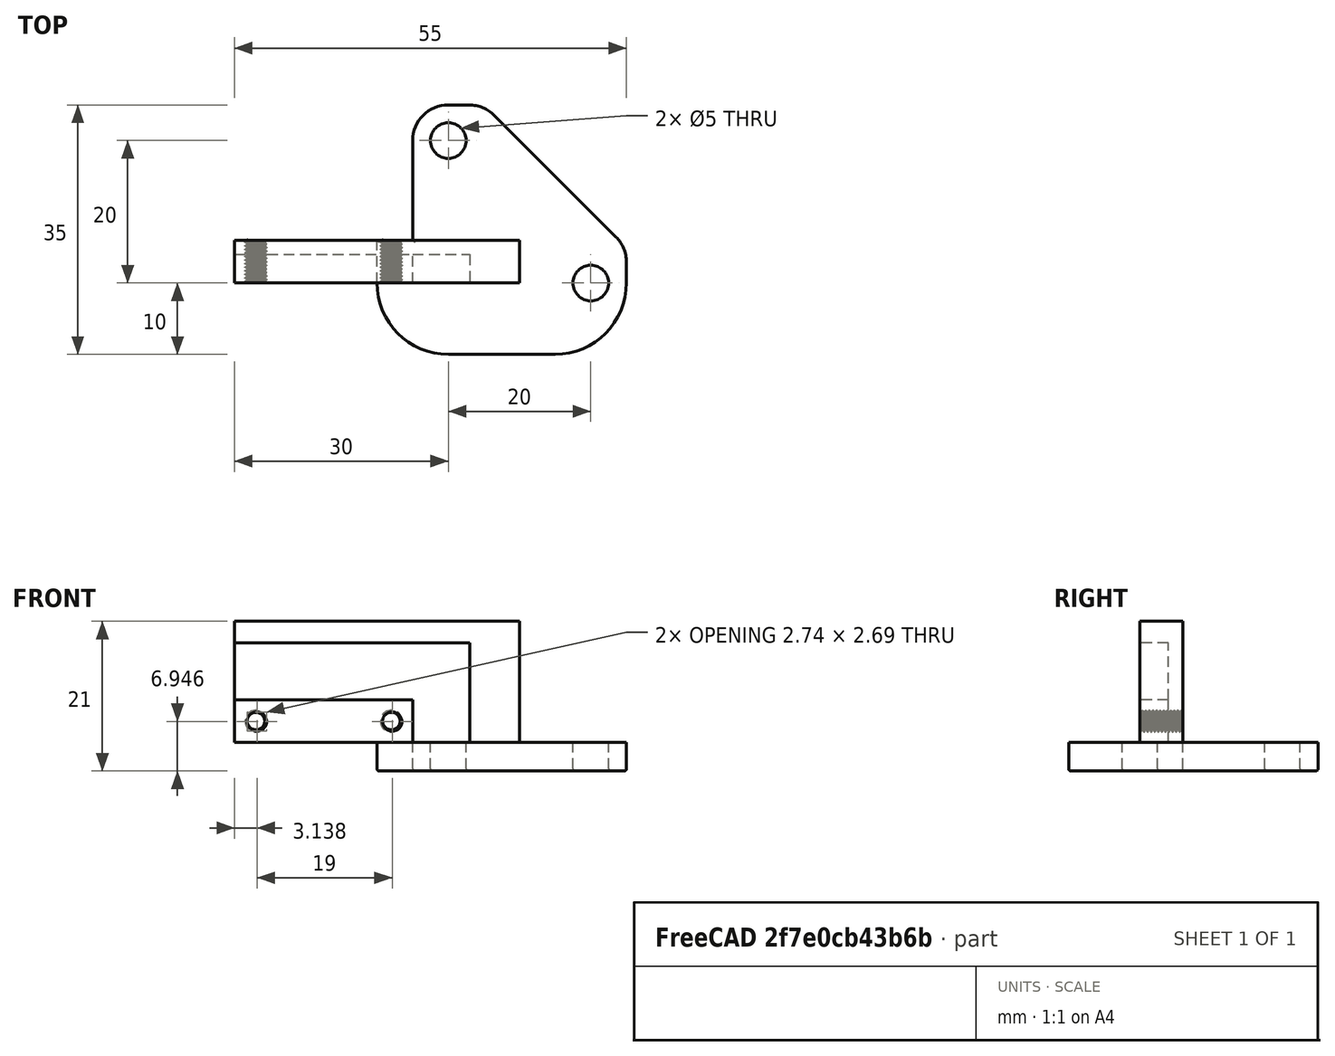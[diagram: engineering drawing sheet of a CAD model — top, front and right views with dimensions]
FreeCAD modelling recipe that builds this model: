
FCSTD DOCUMENT  (FreeCAD 0.18R16146 (Git))
Label: Y_DriveEndschalter_rechts_Ver3
License: All rights reserved
LicenseURL: http://en.wikipedia.org/wiki/All_rights_reserved
objects: Part::Cut×8, Part::Box×6, Part::Fillet×4, Part::Feature×2, Part::Cylinder×2, Part::Chamfer×1, Part::MultiFuse×1
note: 24 computed .brp shape members not serialized (recipe doc carries the construction recipe); baked Part::Feature solids carry a one-line shape summary decoded from their .brp

FEATURE [Part::Box] Box  label="Cube"
  AttacherType = Attacher::AttachEngine3D
  Height = 6
  Length = 40
  Width = 17
FEATURE [Part::Box] Box001  label="Cube001"
  AttacherType = Attacher::AttachEngine3D
  Height = 10
  Length = 33
  Placement = pos=(0,6,2) rot=(0,0,1;0rad)
  Width = 8
FEATURE [Part::Box] Box002  label="Cube002"
  AttacherType = Attacher::AttachEngine3D
  Height = 10
  Length = 8
  Placement = pos=(25,0,2) rot=(0,0,1;0rad)
  Width = 14
FEATURE [Part::Feature] Part__Feature  label="ScrewTap-M3x50_"
  Placement = pos=(3,3,8) rot=(0,0,1;0rad)
  shape: bbox 4.303 x 4.617 x 51.5 mm, 410 faces (baked)
FEATURE [Part::Feature] Part__Feature001  label="ScrewTap-M3x50_001"
  Placement = pos=(22,3,8) rot=(0,0,1;0rad)
  shape: bbox 4.303 x 4.617 x 51.5 mm, 410 faces (baked)
FEATURE [Part::Cut] Cut
  Base = -> Box
  Tool = -> Box001
FEATURE [Part::Cut] Cut001
  Base = -> Cut
  Tool = -> Box002
FEATURE [Part::Cut] Cut002
  Base = -> Cut001
  Tool = -> Part__Feature001
FEATURE [Part::Cut] Cut003
  Base = -> Cut002
  Placement = pos=(-10,16,4) rot=(1,0,0;1.5708rad)
  Tool = -> Part__Feature
FEATURE [Part::Box] Box003  label="Cube003"
  AttacherType = Attacher::AttachEngine3D
  Height = 4
  Length = 45
  Width = 35
FEATURE [Part::Cylinder] Cylinder
  Angle = 360
  AttacherType = Attacher::AttachEngine3D
  Height = 10
  Placement = pos=(40,10,0) rot=(0,0,1;0rad)
  Radius = 2.5
FEATURE [Part::Cylinder] Cylinder001
  Angle = 360
  AttacherType = Attacher::AttachEngine3D
  Height = 10
  Placement = pos=(20,30,0) rot=(0,0,1;0rad)
  Radius = 2.5
FEATURE [Part::Box] Box004  label="Cube004"
  AttacherType = Attacher::AttachEngine3D
  Height = 10
  Length = 15
  Placement = pos=(0,16,0) rot=(0,0,1;0rad)
  Width = 19
FEATURE [Part::Cut] Cut004
  Base = -> Box003
  Tool = -> Box004
FEATURE [Part::Chamfer] Chamfer
  Base = -> Cut004
  Edges = 1 edges r=20: [Edge18]
FEATURE [Part::Fillet] Fillet
  Base = -> Chamfer
  Edges = 2 edges r=10: [Edge15,Edge20]
FEATURE [Part::Fillet] Fillet001
  Base = -> Fillet
  Edges = 3 edges r=5: [Edge11,Edge16,Edge20]
FEATURE [Part::Cut] Cut005
  Base = -> Fillet001
  Tool = -> Cylinder001
FEATURE [Part::Cut] Cut006
  Base = -> Cut005
  Tool = -> Cylinder
FEATURE [Part::Box] Box005  label="Cube005"
  AttacherType = Attacher::AttachEngine3D
  Height = 4
  Length = 10
  Width = 16
FEATURE [Part::Cut] Cut007
  Base = -> Cut006
  Tool = -> Box005
FEATURE [Part::Fillet] Fillet002
  Base = -> Cut007
  Edges = 1 edges r=10: [Edge20]
FEATURE [Part::Fillet] Fillet003
  Base = -> Fillet002
  Edges = 14 edges r=0.3: [Edge15,Edge18,Edge20,Edge23,Edge25,Edge27,Edge28,Edge31,Edge32,Edge34,Edge36,Edge38,Edge40,Edge42]
FEATURE [Part::MultiFuse] Fusion
  Shapes = -> [Cut003,Fillet003]
